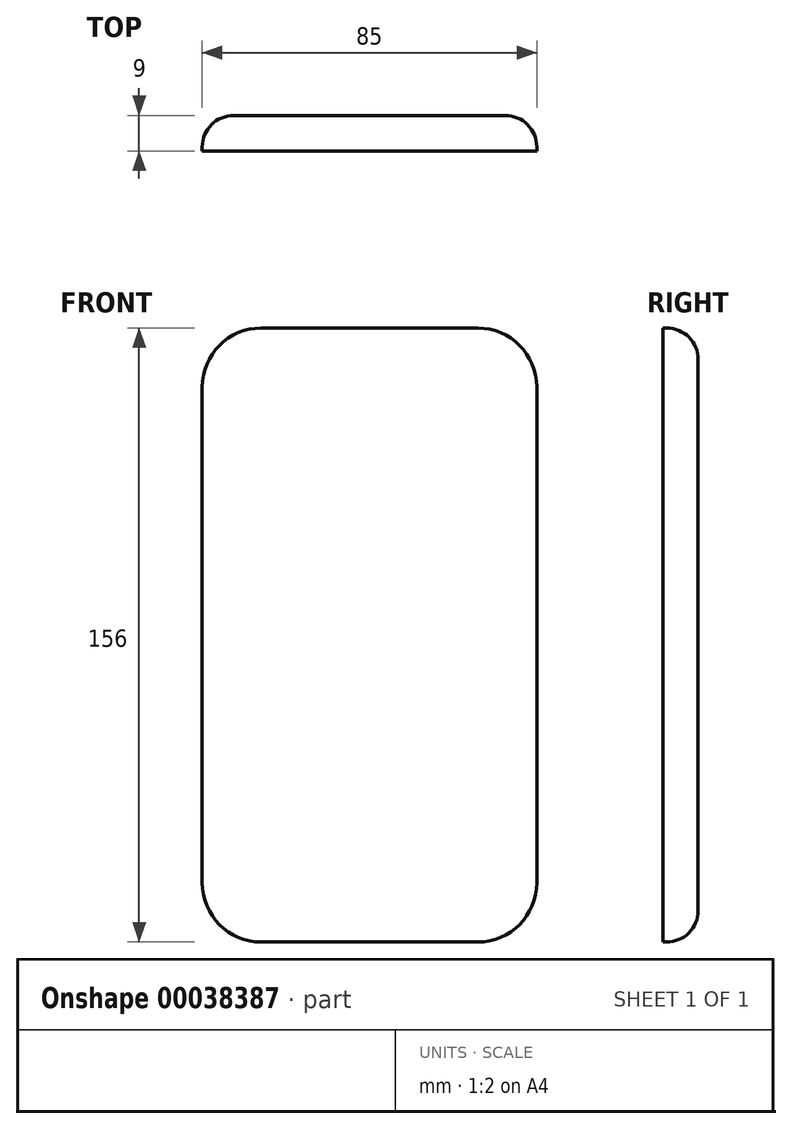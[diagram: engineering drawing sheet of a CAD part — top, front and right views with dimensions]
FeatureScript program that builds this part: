
annotation { "Feature Type Name" : "Feature", "Feature Type Description" : "" }
export const myFeature = defineFeature(function(context is Context, id is Id, definition is map)
    precondition{}
    {
        {
            var Q0;
            Q0=qCreatedBy(makeId("Front.planeOp"),FACE);
            var sketch = newSketch(context, id + "F0", { "sketchPlane" : qUnion([Q0])});
            skLineSegment(sketch, "E0.rect.bottom", {"start": v(-27.5, -78) * mm, "end": v(27.5, -78) * mm});
            skLineSegment(sketch, "E0.rect.top", {"start": v(-27.5, 78) * mm, "end": v(27.5, 78) * mm});
            skLineSegment(sketch, "E0.rect.left", {"start": v(-42.5, -63) * mm, "end": v(-42.5, 63) * mm});
            skLineSegment(sketch, "E0.rect.right", {"start": v(42.5, -63) * mm, "end": v(42.5, 63) * mm});
            skPoint(sketch, "E0.rect.middle", {"position": v(0, 0) * mm});
            skPoint(sketch, "E1.visualSharp", {"position": v(-42.5, 78) * mm});
            skArc(sketch, "E1.filletArc", {"start": v(-27.5, 78) * mm, "mid": v(-38.1, 73.6) * mm, "end": v(-42.5, 63) * mm});
            skPoint(sketch, "E2.visualSharp", {"position": v(42.5, 78) * mm});
            skArc(sketch, "E2.filletArc", {"start": v(42.5, 63) * mm, "mid": v(38.1, 73.6) * mm, "end": v(27.5, 78) * mm});
            skPoint(sketch, "E3.visualSharp", {"position": v(42.5, -78) * mm});
            skArc(sketch, "E3.filletArc", {"start": v(27.5, -78) * mm, "mid": v(38.1, -73.6) * mm, "end": v(42.5, -63) * mm});
            skPoint(sketch, "E4.visualSharp", {"position": v(-42.5, -78) * mm});
            skArc(sketch, "E4.filletArc", {"start": v(-42.5, -63) * mm, "mid": v(-38.1, -73.6) * mm, "end": v(-27.5, -78) * mm});
            skSolve(sketch);
        }
        {
            var Q0;
            Q0 = qSketchRegion(id + "F0", true);
            extrude(context, id + "F1", {"entities" : qUnion([Q0]), "depth" : 9 * mm});
        }
        {
            var Q0;
            Q0=makeQuery(id+"F1.opExtrude","CAP_FACE",FACE,{"disambiguationData":[OSD([sQuery(id+"F0.wireOp",EDGE,"E0.rect.bottom"),sQuery(id+"F0.wireOp",EDGE,"E0.rect.top"),sQuery(id+"F0.wireOp",EDGE,"E0.rect.left"),sQuery(id+"F0.wireOp",EDGE,"E0.rect.right"),sQuery(id+"F0.wireOp",EDGE,"E1.filletArc"),sQuery(id+"F0.wireOp",EDGE,"E2.filletArc"),sQuery(id+"F0.wireOp",EDGE,"E3.filletArc"),sQuery(id+"F0.wireOp",EDGE,"E4.filletArc")])],"isStart":true});
            fillet(context, id + "F2", {"entities" : qUnion([Q0]), "radius" : 8 * mm, "tangentPropagation" : true, "allowEdgeOverflow" : false});
        }
    });
